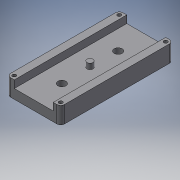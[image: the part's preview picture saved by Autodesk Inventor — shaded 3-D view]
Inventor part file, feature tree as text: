
AUTODESK INVENTOR PART (.ipt)
format: ipt  version: 2019 (Build 230136000, 136)  size: 194,560 bytes
history: native  units: mm
features: sketch x7, extrude x5, hole x2, fillet x1
ambient origin geometry x8: Origin, YZ Plane, XZ Plane, XY Plane, X Axis, Y Axis, Z Axis, Center Point
bodies: Solid1 (feature_tree)
feature tree (15):
  extrude  "Extrusion1"  Depth=28.763mm
  extrude  "Extrusion2"  Depth=4.0mm
  extrude  "Extrusion3"  Depth=4.0mm TaperAngle=0.0deg
  hole  "Hole1"  [1 undecoded]
  extrude  "Extrusion4"  Depth=2.0mm
  extrude  "Extrusion5"  Depth=2.0mm
  hole  "Hole2"  [1 undecoded]
  fillet  "Fillet1"  Radius=3.0mm
  sketch  "Sketch1"  dims[d0=60.0mm d1=28.763mm]
  sketch  "Sketch2"  dims[d2=5.0mm d3=0.0mm d4=4.0mm]
  sketch  "Sketch3"  dims[d5=4.0mm d6=4.0mm d7=0.0mm]
  sketch  "Sketch4"  dims[d8=3.175mm d9=3.0mm d10=0.0mm]
  sketch  "Sketch5"  dims[d11=4.305mm d12=6.0mm d13=7.087mm d14=2.0mm d15=14.3117mm d16=8.0mm d17=20.594885mm d18=2.0mm]
  sketch  "Sketch7"  dims[d19=2.0mm d20=2.0mm]
  sketch  "Sketch8"  dims[d21=3.0mm d22=0.0mm d23=2.0mm d25=3.0mm d26=20.0mm d27=20.0mm d28=0.0mm d29=4.915mm d30=6.0mm d31=8.433mm d32=2.0mm d33=14.3117mm d34=8.0mm d35=20.594885mm]
note: 2 required parameter values undecoded (feature->parameter linkage not recoverable at this tier; creation-order binding heuristic only, values carry confidence <= 0.55)
